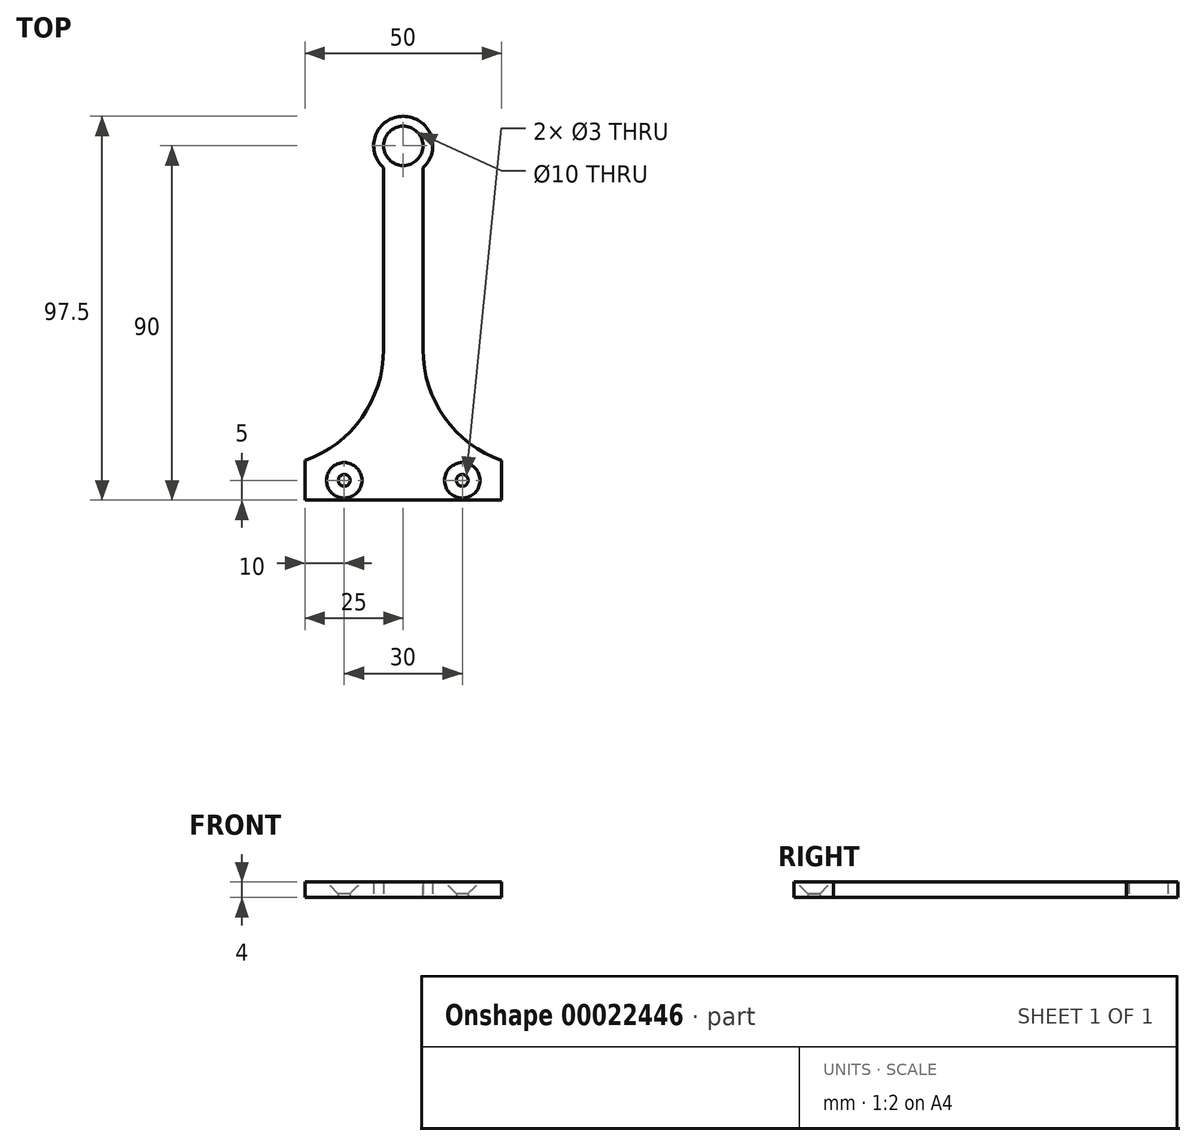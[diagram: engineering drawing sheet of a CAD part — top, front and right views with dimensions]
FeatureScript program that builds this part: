
annotation { "Feature Type Name" : "Feature", "Feature Type Description" : "" }
export const myFeature = defineFeature(function(context is Context, id is Id, definition is map)
    precondition{}
    {
        {
            var Q0;
            Q0=qCreatedBy(makeId("Top.planeOp"),FACE);
            var sketch = newSketch(context, id + "F0", { "sketchPlane" : qUnion([Q0])});
            skLineSegment(sketch, "E0.bottom", {"start": v(0, 0) * mm, "end": v(10, 0) * mm});
            skLineSegment(sketch, "E0.top", {"start": v(0, 90) * mm, "end": v(10, 90) * mm});
            skLineSegment(sketch, "E0.left", {"start": v(0, 0) * mm, "end": v(0, 90) * mm});
            skLineSegment(sketch, "E0.right", {"start": v(10, 0) * mm, "end": v(10, 90) * mm});
            skLineSegment(sketch, "E1.bottom", {"start": v(0, 0) * mm, "end": v(-20, 0) * mm});
            skLineSegment(sketch, "E1.top", {"start": v(0, 10) * mm, "end": v(-20, 10) * mm});
            skLineSegment(sketch, "E1.left", {"start": v(0, 0) * mm, "end": v(0, 10) * mm});
            skLineSegment(sketch, "E1.right", {"start": v(-20, 0) * mm, "end": v(-20, 10) * mm});
            skLineSegment(sketch, "E2.bottom", {"start": v(10, 0) * mm, "end": v(30, 0) * mm});
            skLineSegment(sketch, "E2.top", {"start": v(10, 10) * mm, "end": v(30, 10) * mm});
            skLineSegment(sketch, "E2.left", {"start": v(10, 0) * mm, "end": v(10, 10) * mm});
            skLineSegment(sketch, "E2.right", {"start": v(30, 0) * mm, "end": v(30, 10) * mm});
            skCircle(sketch, "E3", {"center": v(5, 90) * mm, "radius": 5 * mm});
            skCircle(sketch, "E4", {"center": v(5, 90) * mm, "radius": 7.5 * mm});
            skLineSegment(sketch, "E5", {"start": v(-20, 10) * mm, "end": v(0, 0) * mm});
            skLineSegment(sketch, "E6", {"start": v(10, 0) * mm, "end": v(30, 10) * mm});
            skCircle(sketch, "E7", {"center": v(-10, 5) * mm, "radius": 1.5 * mm});
            skCircle(sketch, "E8", {"center": v(20, 5) * mm, "radius": 1.5 * mm});
            skLineSegment(sketch, "E9", {"start": v(0, 10) * mm, "end": v(10, 10) * mm});
            skLineSegment(sketch, "E10", {"start": v(0, 45) * mm, "end": v(10, 45) * mm});
            skSolve(sketch);
        }
        {
            var Q0;
            {var subQ5=sQuery(id+"F0.wireOp",EDGE,"E1.top");Q0=makeQuery(id+"F0.imprint","IMPRINT",FACE,{"disambiguationData":[TD([[makeQuery(id+"F0.imprint","IMPRINT",EDGE,{"derivedFrom":subQ5}),1.0]])]});}
            var Q1;
            {var subQ4=sQuery(id+"F0.wireOp",EDGE,"E1.bottom");Q1=makeQuery(id+"F0.imprint","IMPRINT",FACE,{"disambiguationData":[TD([[makeQuery(id+"F0.imprint","IMPRINT",EDGE,{"derivedFrom":subQ4}),-1.0]])]});}
            var Q2;
            {var subQ4=sQuery(id+"F0.wireOp",EDGE,"E2.top");Q2=makeQuery(id+"F0.imprint","IMPRINT",FACE,{"disambiguationData":[TD([[makeQuery(id+"F0.imprint","IMPRINT",EDGE,{"derivedFrom":subQ4}),-1.0]])]});}
            var Q3;
            {var subQ5=sQuery(id+"F0.wireOp",EDGE,"E2.bottom");Q3=makeQuery(id+"F0.imprint","IMPRINT",FACE,{"disambiguationData":[TD([[makeQuery(id+"F0.imprint","IMPRINT",EDGE,{"derivedFrom":subQ5}),1.0]])]});}
            var Q4;
            Q4=makeQuery(id+"F0.imprint","IMPRINT",FACE,{"disambiguationData":[TD([[makeQuery(id+"F0.imprint","IMPRINT",EDGE,{"derivedFrom":sQuery(id+"F0.wireOp",EDGE,"E0.bottom")}),1.0]])]});
            var Q5;
            {var subQ1=sQuery(id+"F0.wireOp",EDGE,"E9");Q5=makeQuery(id+"F0.imprint","IMPRINT",FACE,{"disambiguationData":[TD([[makeQuery(id+"F0.imprint","IMPRINT",EDGE,{"derivedFrom":subQ1}),1.0]])]});}
            var Q6;
            {var subQ0=sQuery(id+"F0.wireOp",EDGE,"E10");Q6=makeQuery(id+"F0.imprint","IMPRINT",FACE,{"disambiguationData":[TD([[makeQuery(id+"F0.imprint","IMPRINT",EDGE,{"derivedFrom":subQ0}),1.0]])]});}
            var Q7;
            {var subQ0=sQuery(id+"F0.wireOp",EDGE,"E4");var subQ3=sQuery(id+"F0.wireOp",EDGE,"E0.left");var subQ4=makeQuery(id+"F0.imprint","INTERSECT",VERTEX,{"derivedFrom":[subQ3,subQ0]});Q7=makeQuery(id+"F0.imprint","IMPRINT",FACE,{"disambiguationData":[TD([[makeQuery(id+"F0.imprint","IMPRINT",EDGE,{"disambiguationData":[TD([[subQ4,1.0]])],"derivedFrom":subQ0}),1.0]])]});}
            var Q8;
            {var subQ0=sQuery(id+"F0.wireOp",EDGE,"E4");var subQ3=sQuery(id+"F0.wireOp",EDGE,"E0.left");var subQ4=makeQuery(id+"F0.imprint","INTERSECT",VERTEX,{"derivedFrom":[subQ3,subQ0]});Q8=makeQuery(id+"F0.imprint","IMPRINT",FACE,{"disambiguationData":[TD([[makeQuery(id+"F0.imprint","IMPRINT",EDGE,{"disambiguationData":[TD([[subQ4,-1.0]])],"derivedFrom":subQ0}),1.0]])]});}
            extrude(context, id + "F1", {"entities" : qUnion([Q0, Q1, Q2, Q3, Q4, Q5, Q6, Q7, Q8]), "depth" : 4 * mm});
        }
        {
            var Q0;
            Q0=makeQuery(id+"F1.opExtrude","CAP_EDGE",EDGE,{"disambiguationData":[OSD([sQuery(id+"F0.wireOp",EDGE,"E7")])],"isStart":false});
            var Q1;
            Q1=makeQuery(id+"F1.opExtrude","CAP_EDGE",EDGE,{"disambiguationData":[OSD([sQuery(id+"F0.wireOp",EDGE,"E8")])],"isStart":false});
            chamfer(context, id + "F2", {"entities" : qUnion([Q0, Q1]), "width" : 3 * mm, "tangentPropagation" : true});
        }
        {
            var Q0;
            Q0=makeQuery(id+"F1.opExtrude","SWEPT_EDGE",EDGE,{"disambiguationData":[OSD([sQuery(id+"F0.wireOp",EDGE,"E0.right"),sQuery(id+"F0.wireOp",EDGE,"E2.top"),sQuery(id+"F0.wireOp",EDGE,"E2.left")])]});
            var Q1;
            Q1=makeQuery(id+"F1.opExtrude","SWEPT_EDGE",EDGE,{"disambiguationData":[OSD([sQuery(id+"F0.wireOp",EDGE,"E0.left"),sQuery(id+"F0.wireOp",EDGE,"E1.top"),sQuery(id+"F0.wireOp",EDGE,"E1.left"),sQuery(id+"F0.wireOp",EDGE,"E9")])]});
            fillet(context, id + "F3", {"entities" : qUnion([Q0, Q1]), "radius" : 30 * mm, "tangentPropagation" : true, "allowEdgeOverflow" : false});
        }
    });
